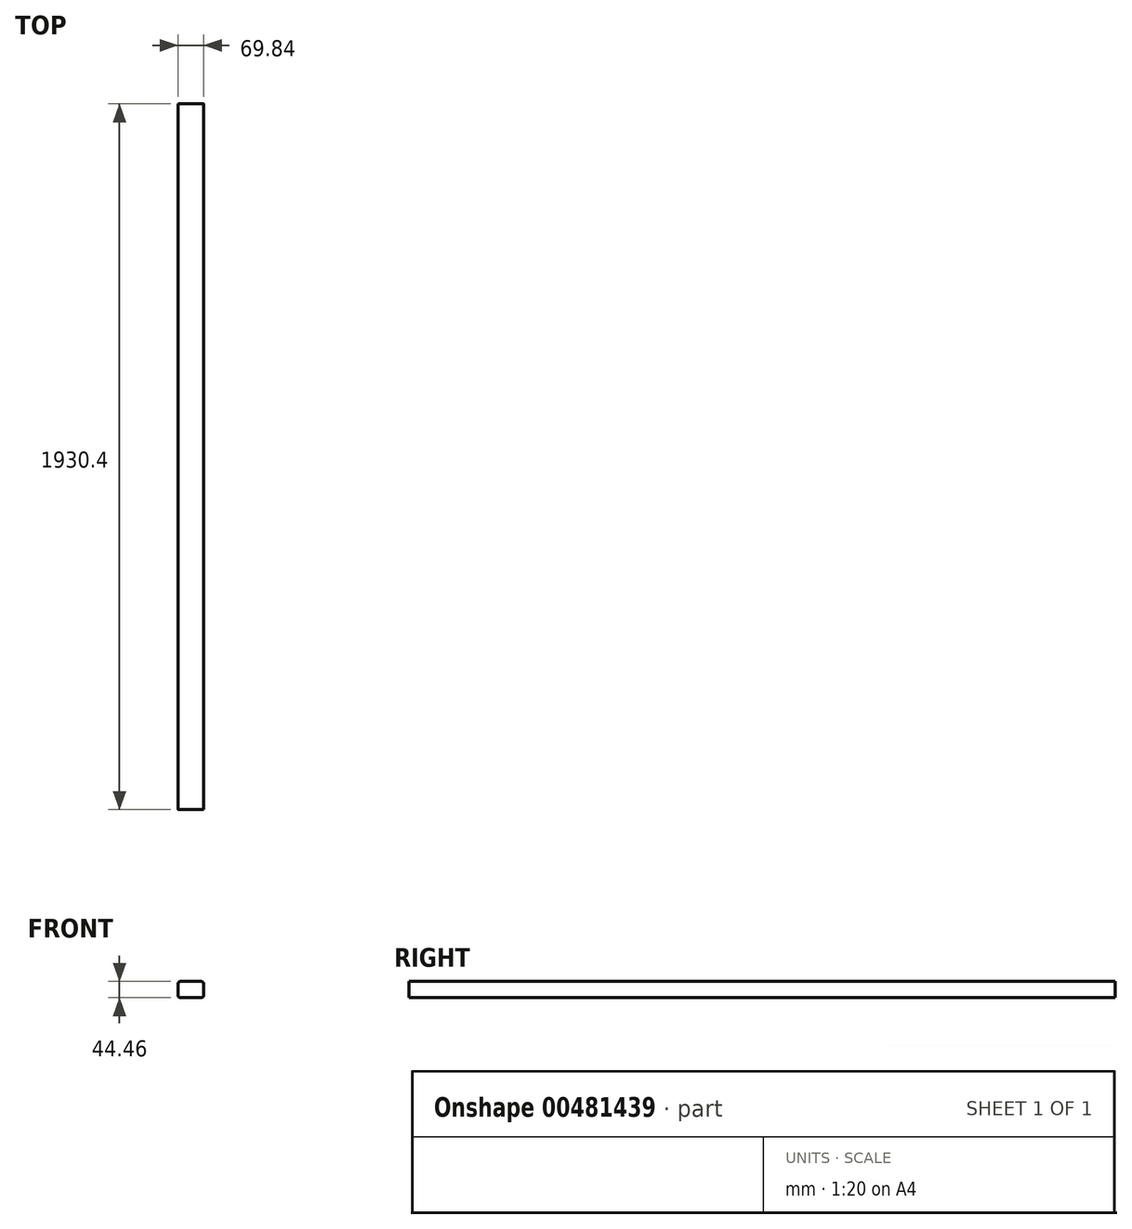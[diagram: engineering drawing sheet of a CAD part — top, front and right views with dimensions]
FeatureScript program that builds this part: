
annotation { "Feature Type Name" : "Feature", "Feature Type Description" : "" }
export const myFeature = defineFeature(function(context is Context, id is Id, definition is map)
    precondition{}
    {
        {
            var Q0;
            Q0=qCreatedBy(makeId("Front.planeOp"),FACE);
            var sketch = newSketch(context, id + "F0", { "sketchPlane" : qUnion([Q0])});
            skLineSegment(sketch, "E0.bottom", {"start": v(28.58, 22.23) * mm, "end": v(-28.58, 22.23) * mm});
            skLineSegment(sketch, "E0.top", {"start": v(28.57, -22.23) * mm, "end": v(-28.57, -22.23) * mm});
            skLineSegment(sketch, "E0.left", {"start": v(34.93, 15.88) * mm, "end": v(34.93, -15.87) * mm});
            skLineSegment(sketch, "E0.right", {"start": v(-34.93, 15.88) * mm, "end": v(-34.93, -15.87) * mm});
            skPoint(sketch, "E0.middle", {"position": v(0, 0) * mm});
            skPoint(sketch, "E1.visualSharp", {"position": v(34.93, 22.23) * mm});
            skArc(sketch, "E1.filletArc", {"start": v(34.93, 15.88) * mm, "mid": v(33.07, 20.37) * mm, "end": v(28.58, 22.22) * mm});
            skPoint(sketch, "E2.visualSharp", {"position": v(-34.93, 22.23) * mm});
            skArc(sketch, "E2.filletArc", {"start": v(-28.58, 22.23) * mm, "mid": v(-33.07, 20.37) * mm, "end": v(-34.93, 15.88) * mm});
            skPoint(sketch, "E3.visualSharp", {"position": v(-34.93, -22.23) * mm});
            skArc(sketch, "E3.filletArc", {"start": v(-34.93, -15.87) * mm, "mid": v(-33.07, -20.37) * mm, "end": v(-28.57, -22.22) * mm});
            skPoint(sketch, "E4.visualSharp", {"position": v(34.93, -22.23) * mm});
            skArc(sketch, "E4.filletArc", {"start": v(28.57, -22.23) * mm, "mid": v(33.07, -20.37) * mm, "end": v(34.93, -15.87) * mm});
            skSolve(sketch);
        }
        {
            var Q0;
            Q0=makeQuery(id+"F0.imprint","IMPRINT",FACE,{"disambiguationData":[TD([[makeQuery(id+"F0.imprint","IMPRINT",EDGE,{"derivedFrom":sQuery(id+"F0.wireOp",EDGE,"E0.bottom")}),1.0]])]});
            extrude(context, id + "F1", {"entities" : qUnion([Q0]), "depth" : 1930.4 * mm});
        }
    });
